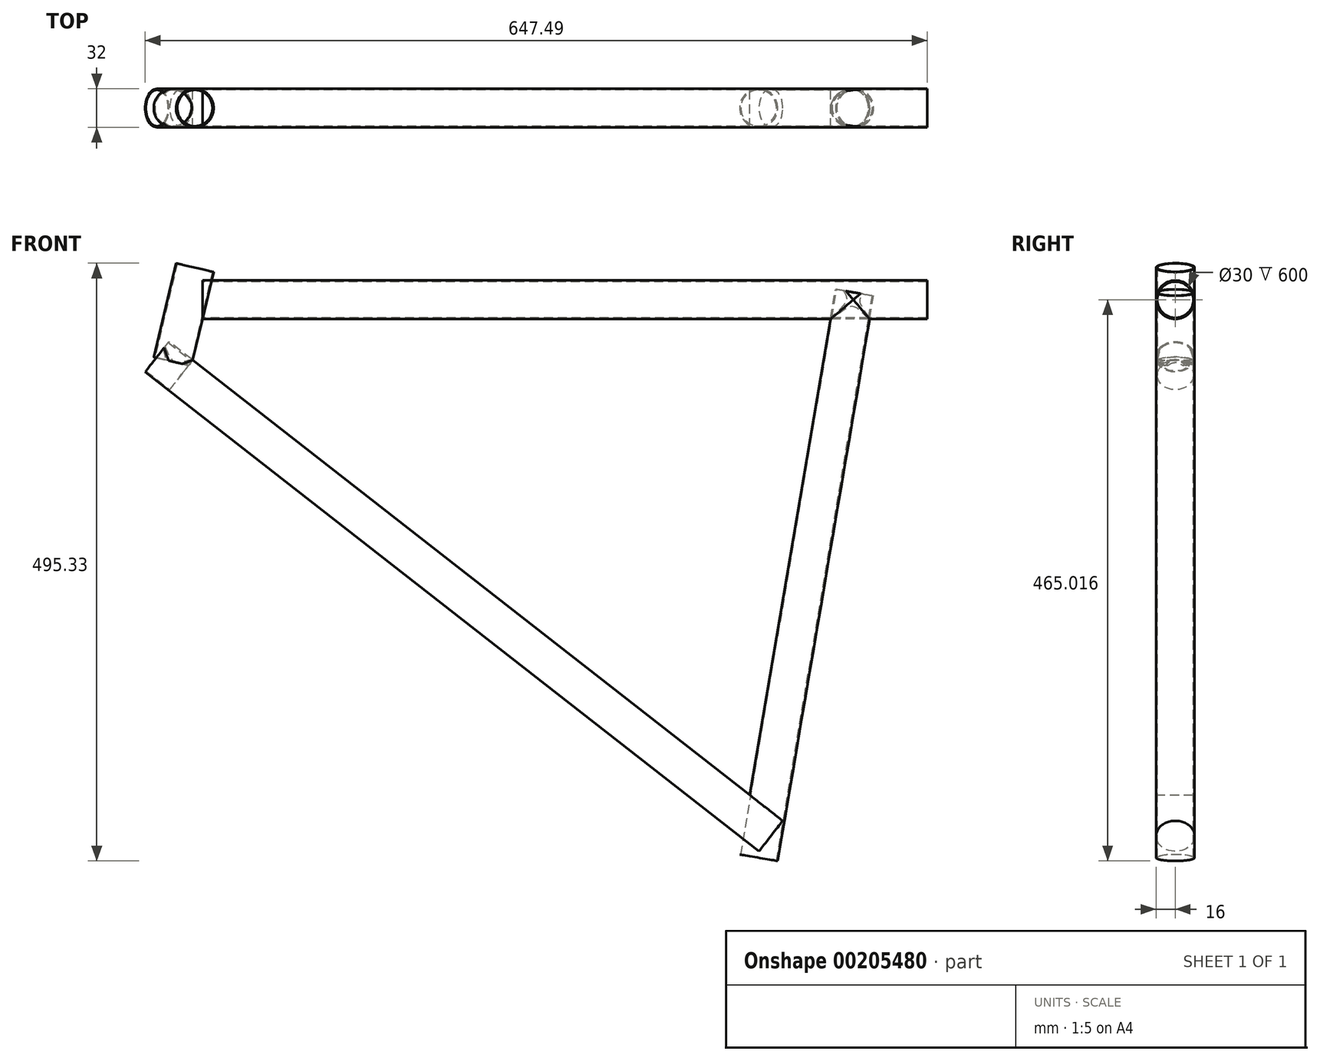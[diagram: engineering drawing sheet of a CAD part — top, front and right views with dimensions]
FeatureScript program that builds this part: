
annotation { "Feature Type Name" : "Feature", "Feature Type Description" : "" }
export const myFeature = defineFeature(function(context is Context, id is Id, definition is map)
    precondition{}
    {
        {
            var Q0;
            Q0=qCreatedBy(makeId("Front.planeOp"),FACE);
            var sketch = newSketch(context, id + "F0", { "sketchPlane" : qUnion([Q0])});
            skLineSegment(sketch, "E0", {"start": v(-67.53, -0.68) * mm, "end": v(452.47, -0.68) * mm});
            skLineSegment(sketch, "E1", {"start": v(452.47, -0.68) * mm, "end": v(385.56, -395.05) * mm});
            skLineSegment(sketch, "E2", {"start": v(385.56, -395.05) * mm, "end": v(-75.61, -34.74) * mm});
            skLineSegment(sketch, "E3", {"start": v(-75.61, -34.74) * mm, "end": v(-67.53, -0.68) * mm});
            skLineSegment(sketch, "E4", {"start": v(-67.53, -0.68) * mm, "end": v(-129.56, 14.05) * mm, "construction": true});
            skLineSegment(sketch, "E5", {"start": v(-75.61, -34.74) * mm, "end": v(-123.59, -96.14) * mm, "construction": true});
            skLineSegment(sketch, "E6", {"start": v(452.47, -0.68) * mm, "end": v(534.08, -14.53) * mm, "construction": true});
            skSolve(sketch);
        }
        {
            var Q0;
            Q0=makeQuery(id+"F0.imprint","IMPRINT",FACE,{"disambiguationData":[TD([[makeQuery(id+"F0.imprint","IMPRINT",EDGE,{"derivedFrom":sQuery(id+"F0.wireOp",EDGE,"E0")}),-1.0]])]});
            extrude(context, id + "F1", {"entities" : qUnion([Q0]), "depth" : 32 * mm});
        }
        {
            var Q0;
            Q0=makeQuery(id+"F1.opExtrude","SWEPT_EDGE",EDGE,{"disambiguationData":[OSD([sQuery(id+"F0.wireOp",EDGE,"E0"),sQuery(id+"F0.wireOp",EDGE,"E3")])]});
            cPlane(context, id + "F2", {"entities" : qUnion([Q0]), "cplaneType" : CPlaneType.LINE_ANGLE, "offset" : 25 * mm, "angle" : 90 * degree, "width" : 150 * mm, "height" : 150 * mm});
        }
        {
            var Q0;
            Q0=qCreatedBy(id+"F2.planeOp",FACE);
            var sketch = newSketch(context, id + "F3", { "sketchPlane" : qUnion([Q0])});
            skCircle(sketch, "E7", {"center": v(-16, 15.32) * mm, "radius": 16 * mm});
            skCircle(sketch, "E8", {"center": v(-16, 15.32) * mm, "radius": 15 * mm});
            skSolve(sketch);
        }
        {
            var Q0;
            Q0 = qSketchRegion(id + "F3", true);
            extrude(context, id + "F4", {"entities" : qUnion([Q0]), "operationType" : NewBodyOperationType.ADD, "depth" : 600 * mm});
        }
        {
            var Q0;
            Q0=sQuery(id+"F0.wireOp",EDGE,"E4");
            cPlane(context, id + "F5", {"entities" : qUnion([Q0]), "cplaneType" : CPlaneType.LINE_ANGLE, "offset" : 25 * mm, "angle" : 90 * degree, "width" : 150 * mm, "height" : 150 * mm});
        }
        {
            var Q0;
            Q0=qCreatedBy(id+"F5.planeOp",FACE);
            var sketch = newSketch(context, id + "F6", { "sketchPlane" : qUnion([Q0])});
            skCircle(sketch, "E9", {"center": v(-81.54, -16) * mm, "radius": 16 * mm});
            skCircle(sketch, "E10", {"center": v(-81.54, -16) * mm, "radius": 15 * mm});
            skSolve(sketch);
        }
        {
            var Q0;
            Q0 = qSketchRegion(id + "F6", true);
            extrude(context, id + "F7", {"entities" : qUnion([Q0]), "endBound" : BoundingType.SYMMETRIC, "depth" : 80 * mm});
        }
        {
            var Q0;
            Q0=sQuery(id+"F0.wireOp",EDGE,"E5");
            cPlane(context, id + "F8", {"entities" : qUnion([Q0]), "cplaneType" : CPlaneType.LINE_ANGLE, "offset" : 25 * mm, "angle" : 0 * degree, "width" : 150 * mm, "height" : 150 * mm});
        }
        {
            var Q0;
            Q0=qCreatedBy(id+"F8.planeOp",FACE);
            var sketch = newSketch(context, id + "F9", { "sketchPlane" : qUnion([Q0])});
            skCircle(sketch, "E11", {"center": v(16, -89.93) * mm, "radius": 16 * mm});
            skCircle(sketch, "E12", {"center": v(16, -89.93) * mm, "radius": 15 * mm});
            skSolve(sketch);
        }
        {
            var Q0;
            Q0=makeQuery(id+"F9.imprint","IMPRINT",FACE,{"disambiguationData":[TD([[makeQuery(id+"F9.imprint","IMPRINT",EDGE,{"derivedFrom":sQuery(id+"F9.wireOp",EDGE,"E12")}),1.0]])]});
            var Q1;
            Q1 = qSketchRegion(id + "F9", true);
            extrude(context, id + "F10", {"entities" : qUnion([Q0, Q1]), "oppositeDirection" : true, "depth" : 620 * mm});
        }
        {
            var Q0;
            Q0 = qSketchRegion(id + "F9", true);
            extrude(context, id + "F11", {"entities" : qUnion([Q0]), "operationType" : NewBodyOperationType.ADD, "depth" : 25 * mm});
        }
        {
            var Q0;
            Q0=sQuery(id+"F0.wireOp",EDGE,"E6");
            cPlane(context, id + "F12", {"entities" : qUnion([Q0]), "cplaneType" : CPlaneType.LINE_ANGLE, "offset" : 25 * mm, "angle" : 90 * degree, "width" : 150 * mm, "height" : 150 * mm});
        }
        {
            var Q0;
            Q0=qCreatedBy(id+"F12.planeOp",FACE);
            var sketch = newSketch(context, id + "F13", { "sketchPlane" : qUnion([Q0])});
            skCircle(sketch, "E13", {"center": v(462.21, -16) * mm, "radius": 16 * mm});
            skCircle(sketch, "E14", {"center": v(462.21, -16) * mm, "radius": 15 * mm});
            skSolve(sketch);
        }
        {
            var Q0;
            Q0 = qSketchRegion(id + "F13", true);
            extrude(context, id + "F14", {"entities" : qUnion([Q0]), "oppositeDirection" : true, "depth" : 450 * mm});
        }
        {
            var Q0;
            Q0 = qSketchRegion(id + "F13", true);
            extrude(context, id + "F15", {"entities" : qUnion([Q0]), "operationType" : NewBodyOperationType.ADD, "depth" : 25 * mm});
        }
    });
